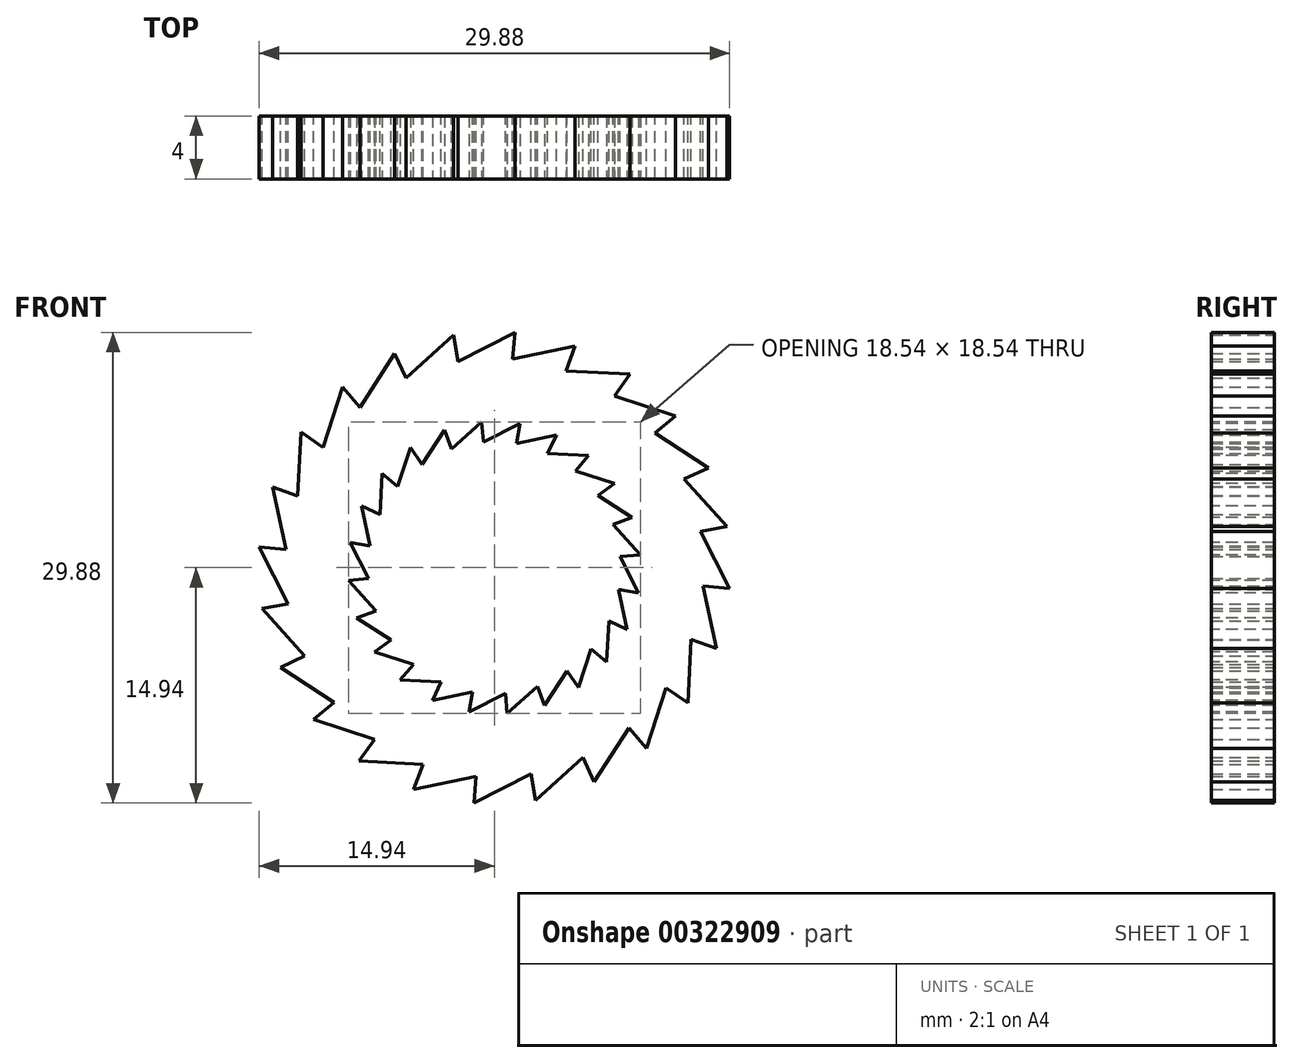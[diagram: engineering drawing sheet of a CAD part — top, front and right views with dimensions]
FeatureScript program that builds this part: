
annotation { "Feature Type Name" : "Feature", "Feature Type Description" : "" }
export const myFeature = defineFeature(function(context is Context, id is Id, definition is map)
    precondition{}
    {
        {
            var Q0;
            Q0=qCreatedBy(makeId("Front.planeOp"),FACE);
            var sketch = newSketch(context, id + "F0", { "sketchPlane" : qUnion([Q0])});
            skCircle(sketch, "E0", {"center": v(0, 0) * mm, "radius": 13 * mm, "construction": true});
            skLineSegment(sketch, "E1", {"start": v(0, 13) * mm, "end": v(5.13, 14.1) * mm});
            skLineSegment(sketch, "E2", {"start": v(5.13, 14.1) * mm, "end": v(4.45, 12.22) * mm});
            skCircle(sketch, "E3", {"center": v(0, 0) * mm, "radius": 10 * mm, "construction": true});
            skLineSegment(sketch, "E4", {"start": v(0, 0) * mm, "end": v(1.74, 9.85) * mm, "construction": true});
            skLineSegment(sketch, "E5", {"start": v(0, 0) * mm, "end": v(0, 13) * mm, "construction": true});
            skLineSegment(sketch, "E6", {"start": v(0, 0) * mm, "end": v(5, 8.66) * mm, "construction": true});
            skLineSegment(sketch, "E7", {"start": v(1.4, 7.89) * mm, "end": v(5, 8.66) * mm});
            skLineSegment(sketch, "E8", {"start": v(0, 13) * mm, "end": v(1.74, 9.85) * mm});
            skLineSegment(sketch, "E9", {"start": v(4.45, 12.22) * mm, "end": v(5, 8.66) * mm});
            skLineSegment(sketch, "E10.trimOffspring", {"start": v(3, 8.23) * mm, "end": v(0, 0) * mm, "construction": true});
            skLineSegment(sketch, "E11", {"start": v(1.74, 9.85) * mm, "end": v(1.4, 7.89) * mm});
            skSolve(sketch);
        }
        {
            var Q0;
            Q0=makeQuery(id+"F0.imprint","IMPRINT",FACE,{"disambiguationData":[TD([[makeQuery(id+"F0.imprint","IMPRINT",EDGE,{"derivedFrom":sQuery(id+"F0.wireOp",EDGE,"E1")}),-1.0]])]});
            extrude(context, id + "F1", {"entities" : qUnion([Q0]), "depth" : 4 * mm});
        }
        {
            var Q0;
            Q0=makeQuery(id+"F1.opExtrude","SWEPT_BODY",BODY,{"disambiguationData":[OSD([sQuery(id+"F0.wireOp",EDGE,"E1"),sQuery(id+"F0.wireOp",EDGE,"E2"),sQuery(id+"F0.wireOp",EDGE,"E7"),sQuery(id+"F0.wireOp",EDGE,"E8"),sQuery(id+"F0.wireOp",EDGE,"E9"),sQuery(id+"F0.wireOp",EDGE,"E11")])]});
            var Q1;
            Q1=sQuery(id+"F0.wireOp",EDGE,"E3");
            circularPattern(context, id + "F2", {"operationType" : NewBodyOperationType.ADD, "entities" : qUnion([Q0]), "axis" : qUnion([Q1]), "angle" : 360 * degree, "instanceCount" : 24, "equalSpace" : true});
        }
    });
